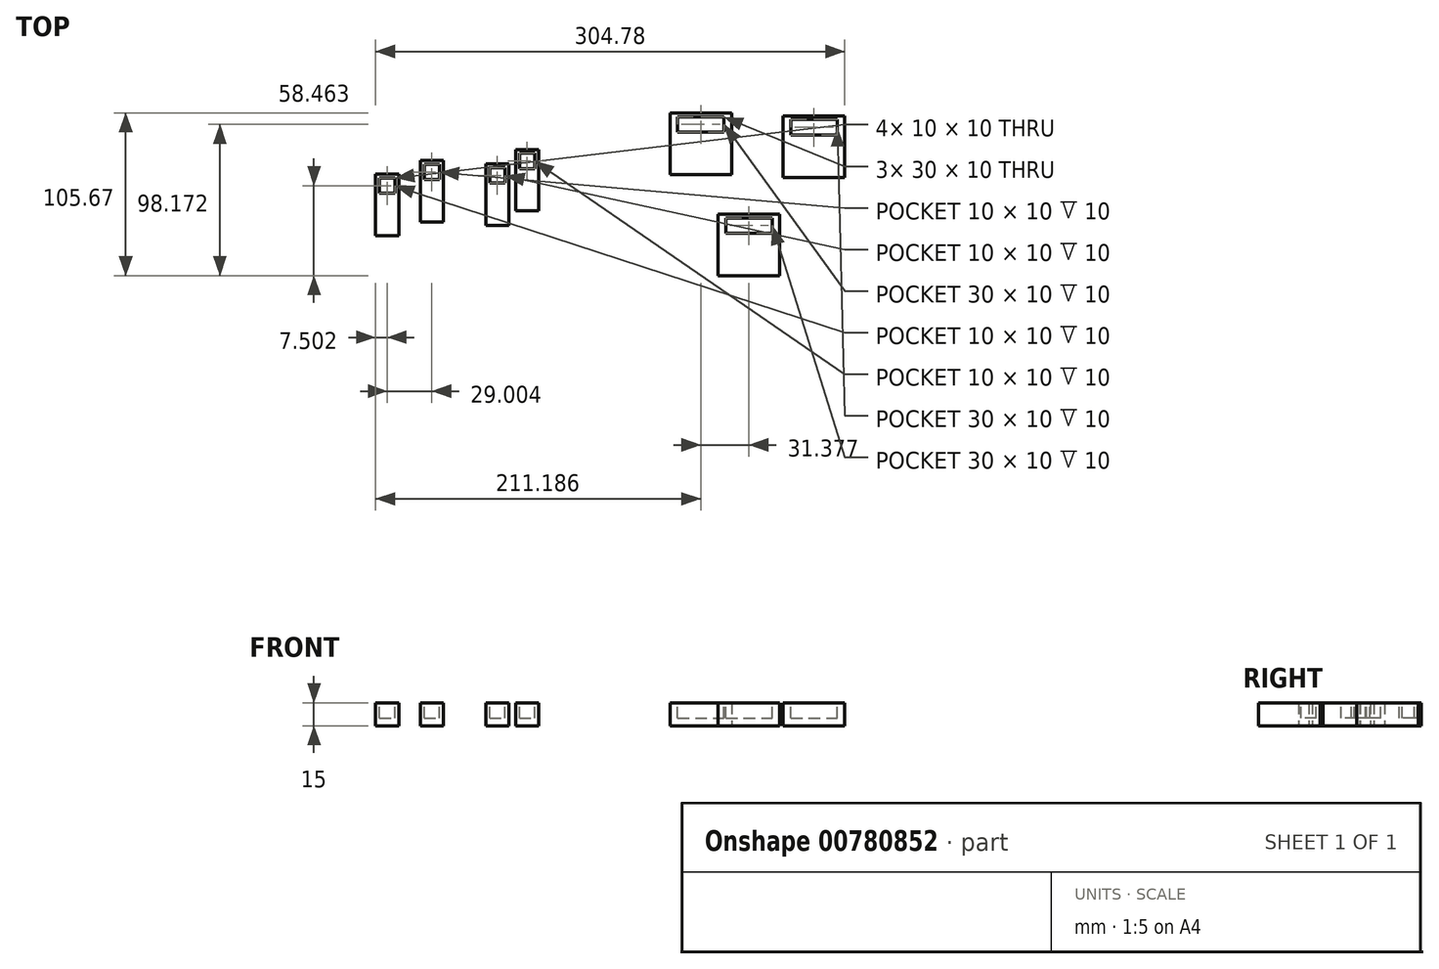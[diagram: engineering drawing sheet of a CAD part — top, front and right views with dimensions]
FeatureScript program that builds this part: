
annotation { "Feature Type Name" : "Feature", "Feature Type Description" : "" }
export const myFeature = defineFeature(function(context is Context, id is Id, definition is map)
    precondition{}
    {
        {
            var Q0;
            Q0=qCreatedBy(makeId("Top.planeOp"),FACE);
            var sketch = newSketch(context, id + "F0", { "sketchPlane" : qUnion([Q0])});
            skLineSegment(sketch, "E0.bottom", {"start": v(-61.29, 27.06) * mm, "end": v(-46.29, 27.06) * mm});
            skLineSegment(sketch, "E0.top", {"start": v(-61.29, -12.94) * mm, "end": v(-46.29, -12.94) * mm});
            skLineSegment(sketch, "E0.left", {"start": v(-61.29, 27.06) * mm, "end": v(-61.29, -12.94) * mm});
            skLineSegment(sketch, "E0.right", {"start": v(-46.29, 27.06) * mm, "end": v(-46.29, -12.94) * mm});
            skLineSegment(sketch, "E1.bottom", {"start": v(-32.28, 35.9) * mm, "end": v(-17.28, 35.9) * mm});
            skLineSegment(sketch, "E1.top", {"start": v(-32.28, -4.1) * mm, "end": v(-17.28, -4.1) * mm});
            skLineSegment(sketch, "E1.left", {"start": v(-32.28, 35.9) * mm, "end": v(-32.28, -4.1) * mm});
            skLineSegment(sketch, "E1.right", {"start": v(-17.28, 35.9) * mm, "end": v(-17.28, -4.1) * mm});
            skLineSegment(sketch, "E2.bottom", {"start": v(10.28, 33.75) * mm, "end": v(25.28, 33.75) * mm});
            skLineSegment(sketch, "E2.top", {"start": v(10.28, -6.25) * mm, "end": v(25.28, -6.25) * mm});
            skLineSegment(sketch, "E2.left", {"start": v(10.28, 33.75) * mm, "end": v(10.28, -6.25) * mm});
            skLineSegment(sketch, "E2.right", {"start": v(25.28, 33.75) * mm, "end": v(25.28, -6.25) * mm});
            skLineSegment(sketch, "E3.bottom", {"start": v(29.65, 43.07) * mm, "end": v(44.65, 43.07) * mm});
            skLineSegment(sketch, "E3.top", {"start": v(29.65, 3.07) * mm, "end": v(44.65, 3.07) * mm});
            skLineSegment(sketch, "E3.left", {"start": v(29.65, 43.07) * mm, "end": v(29.65, 3.07) * mm});
            skLineSegment(sketch, "E3.right", {"start": v(44.65, 43.07) * mm, "end": v(44.65, 3.07) * mm});
            skSolve(sketch);
        }
        {
            var Q0;
            Q0 = qSketchRegion(id + "F0", true);
            extrude(context, id + "F1", {"entities" : qUnion([Q0]), "depth" : 15 * mm, "offsetDistance" : 25 * mm});
        }
        {
            var Q0;
            Q0=makeQuery(id+"F1.opExtrude","CAP_FACE",FACE,{"disambiguationData":[OSD([sQuery(id+"F0.wireOp",EDGE,"E0.bottom"),sQuery(id+"F0.wireOp",EDGE,"E0.top"),sQuery(id+"F0.wireOp",EDGE,"E0.left"),sQuery(id+"F0.wireOp",EDGE,"E0.right")])],"isStart":false});
            var sketch = newSketch(context, id + "F2", { "sketchPlane" : qUnion([Q0])});
            skLineSegment(sketch, "E4.bottom", {"start": v(-58.79, 24.56) * mm, "end": v(-48.79, 24.56) * mm});
            skLineSegment(sketch, "E4.top", {"start": v(-58.79, 14.56) * mm, "end": v(-48.79, 14.56) * mm});
            skLineSegment(sketch, "E4.left", {"start": v(-58.79, 24.56) * mm, "end": v(-58.79, 14.56) * mm});
            skLineSegment(sketch, "E4.right", {"start": v(-48.79, 24.56) * mm, "end": v(-48.79, 14.56) * mm});
            skSolve(sketch);
        }
        {
            var Q0;
            Q0=makeQuery(id+"F1.opExtrude","CAP_FACE",FACE,{"disambiguationData":[OSD([sQuery(id+"F0.wireOp",EDGE,"E1.bottom"),sQuery(id+"F0.wireOp",EDGE,"E1.top"),sQuery(id+"F0.wireOp",EDGE,"E1.left"),sQuery(id+"F0.wireOp",EDGE,"E1.right")])],"isStart":false});
            var sketch = newSketch(context, id + "F3", { "sketchPlane" : qUnion([Q0])});
            skLineSegment(sketch, "E5.bottom", {"start": v(-29.78, 33.4) * mm, "end": v(-19.78, 33.4) * mm});
            skLineSegment(sketch, "E5.top", {"start": v(-29.78, 23.4) * mm, "end": v(-19.78, 23.4) * mm});
            skLineSegment(sketch, "E5.left", {"start": v(-29.78, 33.4) * mm, "end": v(-29.78, 23.4) * mm});
            skLineSegment(sketch, "E5.right", {"start": v(-19.78, 33.4) * mm, "end": v(-19.78, 23.4) * mm});
            skSolve(sketch);
        }
        {
            var Q0;
            Q0=makeQuery(id+"F1.opExtrude","CAP_FACE",FACE,{"disambiguationData":[OSD([sQuery(id+"F0.wireOp",EDGE,"E2.bottom"),sQuery(id+"F0.wireOp",EDGE,"E2.top"),sQuery(id+"F0.wireOp",EDGE,"E2.left"),sQuery(id+"F0.wireOp",EDGE,"E2.right")])],"isStart":false});
            var sketch = newSketch(context, id + "F4", { "sketchPlane" : qUnion([Q0])});
            skLineSegment(sketch, "E6.bottom", {"start": v(12.78, 31.25) * mm, "end": v(22.78, 31.25) * mm});
            skLineSegment(sketch, "E6.top", {"start": v(12.78, 21.25) * mm, "end": v(22.78, 21.25) * mm});
            skLineSegment(sketch, "E6.left", {"start": v(12.78, 31.25) * mm, "end": v(12.78, 21.25) * mm});
            skLineSegment(sketch, "E6.right", {"start": v(22.78, 31.25) * mm, "end": v(22.78, 21.25) * mm});
            skSolve(sketch);
        }
        {
            var Q0;
            Q0=makeQuery(id+"F1.opExtrude","CAP_FACE",FACE,{"disambiguationData":[OSD([sQuery(id+"F0.wireOp",EDGE,"E3.bottom"),sQuery(id+"F0.wireOp",EDGE,"E3.top"),sQuery(id+"F0.wireOp",EDGE,"E3.left"),sQuery(id+"F0.wireOp",EDGE,"E3.right")])],"isStart":false});
            var sketch = newSketch(context, id + "F5", { "sketchPlane" : qUnion([Q0])});
            skLineSegment(sketch, "E7.bottom", {"start": v(32.15, 40.57) * mm, "end": v(42.15, 40.57) * mm});
            skLineSegment(sketch, "E7.top", {"start": v(32.15, 30.57) * mm, "end": v(42.15, 30.57) * mm});
            skLineSegment(sketch, "E7.left", {"start": v(32.15, 40.57) * mm, "end": v(32.15, 30.57) * mm});
            skLineSegment(sketch, "E7.right", {"start": v(42.15, 40.57) * mm, "end": v(42.15, 30.57) * mm});
            skSolve(sketch);
        }
        {
            var Q0;
            Q0=makeQuery(id+"F2.imprint","IMPRINT",FACE,{"disambiguationData":[TD([[makeQuery(id+"F2.imprint","IMPRINT",EDGE,{"derivedFrom":sQuery(id+"F2.wireOp",EDGE,"E4.bottom")}),-1.0]])]});
            var Q1;
            Q1=makeQuery(id+"F3.imprint","IMPRINT",FACE,{"disambiguationData":[TD([[makeQuery(id+"F3.imprint","IMPRINT",EDGE,{"derivedFrom":sQuery(id+"F3.wireOp",EDGE,"E5.bottom")}),-1.0]])]});
            var Q2;
            Q2=makeQuery(id+"F4.imprint","IMPRINT",FACE,{"disambiguationData":[TD([[makeQuery(id+"F4.imprint","IMPRINT",EDGE,{"derivedFrom":sQuery(id+"F4.wireOp",EDGE,"E6.bottom")}),-1.0]])]});
            var Q3;
            Q3=makeQuery(id+"F5.imprint","IMPRINT",FACE,{"disambiguationData":[TD([[makeQuery(id+"F5.imprint","IMPRINT",EDGE,{"derivedFrom":sQuery(id+"F5.wireOp",EDGE,"E7.bottom")}),-1.0]])]});
            extrude(context, id + "F6", {"entities" : qUnion([Q0, Q1, Q2, Q3]), "operationType" : NewBodyOperationType.REMOVE, "oppositeDirection" : true, "depth" : 10 * mm, "offsetDistance" : 25 * mm});
        }
        {
            var Q0;
            Q0=makeQuery(id+"F3.imprint","IMPRINT",FACE,{"disambiguationData":[TD([[makeQuery(id+"F3.imprint","IMPRINT",EDGE,{"derivedFrom":sQuery(id+"F3.wireOp",EDGE,"E5.bottom")}),-1.0]])]});
            extrude(context, id + "F7", {"entities" : qUnion([Q0]), "operationType" : NewBodyOperationType.REMOVE, "oppositeDirection" : true, "depth" : 10 * mm, "offsetDistance" : 25 * mm});
        }
        {
            var Q0;
            Q0=makeQuery(id+"F4.imprint","IMPRINT",FACE,{"disambiguationData":[TD([[makeQuery(id+"F4.imprint","IMPRINT",EDGE,{"derivedFrom":sQuery(id+"F4.wireOp",EDGE,"E6.bottom")}),-1.0]])]});
            extrude(context, id + "F8", {"entities" : qUnion([Q0]), "operationType" : NewBodyOperationType.REMOVE, "oppositeDirection" : true, "depth" : 10 * mm, "offsetDistance" : 25 * mm});
        }
        {
            var Q0;
            Q0=makeQuery(id+"F5.imprint","IMPRINT",FACE,{"disambiguationData":[TD([[makeQuery(id+"F5.imprint","IMPRINT",EDGE,{"derivedFrom":sQuery(id+"F5.wireOp",EDGE,"E7.bottom")}),-1.0]])]});
            extrude(context, id + "F9", {"entities" : qUnion([Q0]), "operationType" : NewBodyOperationType.REMOVE, "oppositeDirection" : true, "depth" : 10 * mm, "offsetDistance" : 25 * mm});
        }
        {
            var Q0;
            Q0=qCreatedBy(makeId("Top.planeOp"),FACE);
            var sketch = newSketch(context, id + "F10", { "sketchPlane" : qUnion([Q0])});
            skLineSegment(sketch, "E8.bottom", {"start": v(129.9, 66.77) * mm, "end": v(169.9, 66.77) * mm});
            skLineSegment(sketch, "E8.top", {"start": v(129.9, 26.77) * mm, "end": v(169.9, 26.77) * mm});
            skLineSegment(sketch, "E8.left", {"start": v(129.9, 66.77) * mm, "end": v(129.9, 26.77) * mm});
            skLineSegment(sketch, "E8.right", {"start": v(169.9, 66.77) * mm, "end": v(169.9, 26.77) * mm});
            skLineSegment(sketch, "E9.bottom", {"start": v(203.5, 64.94) * mm, "end": v(243.5, 64.94) * mm});
            skLineSegment(sketch, "E9.top", {"start": v(203.5, 24.94) * mm, "end": v(243.5, 24.94) * mm});
            skLineSegment(sketch, "E9.left", {"start": v(203.5, 64.94) * mm, "end": v(203.5, 24.94) * mm});
            skLineSegment(sketch, "E9.right", {"start": v(243.5, 64.94) * mm, "end": v(243.5, 24.94) * mm});
            skLineSegment(sketch, "E10.bottom", {"start": v(161.27, 1.1) * mm, "end": v(201.27, 1.1) * mm});
            skLineSegment(sketch, "E10.top", {"start": v(161.27, -38.9) * mm, "end": v(201.27, -38.9) * mm});
            skLineSegment(sketch, "E10.left", {"start": v(161.27, 1.1) * mm, "end": v(161.27, -38.9) * mm});
            skLineSegment(sketch, "E10.right", {"start": v(201.27, 1.1) * mm, "end": v(201.27, -38.9) * mm});
            skSolve(sketch);
        }
        {
            var Q0;
            Q0 = qSketchRegion(id + "F10", true);
            extrude(context, id + "F11", {"entities" : qUnion([Q0]), "depth" : 15 * mm, "offsetDistance" : 25 * mm});
        }
        {
            var Q0;
            Q0=makeQuery(id+"F11.opExtrude","CAP_FACE",FACE,{"disambiguationData":[OSD([sQuery(id+"F10.wireOp",EDGE,"E8.bottom"),sQuery(id+"F10.wireOp",EDGE,"E8.top"),sQuery(id+"F10.wireOp",EDGE,"E8.left"),sQuery(id+"F10.wireOp",EDGE,"E8.right")])],"isStart":false});
            var sketch = newSketch(context, id + "F12", { "sketchPlane" : qUnion([Q0])});
            skLineSegment(sketch, "E11.bottom", {"start": v(134.9, 64.27) * mm, "end": v(164.9, 64.27) * mm});
            skLineSegment(sketch, "E11.top", {"start": v(134.9, 54.27) * mm, "end": v(164.9, 54.27) * mm});
            skLineSegment(sketch, "E11.left", {"start": v(134.9, 64.27) * mm, "end": v(134.9, 54.27) * mm});
            skLineSegment(sketch, "E11.right", {"start": v(164.9, 64.27) * mm, "end": v(164.9, 54.27) * mm});
            skLineSegment(sketch, "E12.bottom", {"start": v(208.5, 62.44) * mm, "end": v(238.5, 62.44) * mm});
            skLineSegment(sketch, "E12.top", {"start": v(208.5, 52.44) * mm, "end": v(238.5, 52.44) * mm});
            skLineSegment(sketch, "E12.left", {"start": v(208.5, 62.44) * mm, "end": v(208.5, 52.44) * mm});
            skLineSegment(sketch, "E12.right", {"start": v(238.5, 62.44) * mm, "end": v(238.5, 52.44) * mm});
            skLineSegment(sketch, "E13.bottom", {"start": v(166.27, -1.4) * mm, "end": v(196.27, -1.4) * mm});
            skLineSegment(sketch, "E13.top", {"start": v(166.27, -11.4) * mm, "end": v(196.27, -11.4) * mm});
            skLineSegment(sketch, "E13.left", {"start": v(166.27, -1.4) * mm, "end": v(166.27, -11.4) * mm});
            skLineSegment(sketch, "E13.right", {"start": v(196.27, -1.4) * mm, "end": v(196.27, -11.4) * mm});
            skSolve(sketch);
        }
        {
            var Q0;
            Q0=makeQuery(id+"F12.imprint","IMPRINT",FACE,{"disambiguationData":[TD([[makeQuery(id+"F12.imprint","IMPRINT",EDGE,{"derivedFrom":sQuery(id+"F12.wireOp",EDGE,"E11.bottom")}),-1.0]])]});
            extrude(context, id + "F13", {"entities" : qUnion([Q0]), "operationType" : NewBodyOperationType.REMOVE, "oppositeDirection" : true, "depth" : 10 * mm, "offsetDistance" : 25 * mm});
        }
        {
            var Q0;
            Q0=makeQuery(id+"F12.imprint","IMPRINT",FACE,{"disambiguationData":[TD([[makeQuery(id+"F12.imprint","IMPRINT",EDGE,{"derivedFrom":sQuery(id+"F12.wireOp",EDGE,"E12.bottom")}),-1.0]])]});
            extrude(context, id + "F14", {"entities" : qUnion([Q0]), "operationType" : NewBodyOperationType.REMOVE, "oppositeDirection" : true, "depth" : 10 * mm, "offsetDistance" : 25 * mm});
        }
        {
            var Q0;
            Q0=makeQuery(id+"F12.imprint","IMPRINT",FACE,{"disambiguationData":[TD([[makeQuery(id+"F12.imprint","IMPRINT",EDGE,{"derivedFrom":sQuery(id+"F12.wireOp",EDGE,"E13.bottom")}),-1.0]])]});
            extrude(context, id + "F15", {"entities" : qUnion([Q0]), "operationType" : NewBodyOperationType.REMOVE, "oppositeDirection" : true, "depth" : 10 * mm, "offsetDistance" : 25 * mm});
        }
    });
